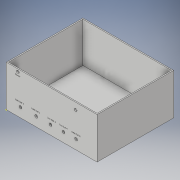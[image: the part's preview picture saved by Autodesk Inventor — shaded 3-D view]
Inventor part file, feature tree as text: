
AUTODESK INVENTOR PART (.ipt)
format: ipt  version: 2019 (Build 230136000, 136)  size: 162,816 bytes
history: native  units: in
note: dims shown in document units (in); Inventor stores cm internally (conversion verified against a paired STEP export)
features: sketch x11, extrude x6, hole x2
ambient origin geometry x8: Origin, YZ Plane, XZ Plane, XY Plane, X Axis, Y Axis, Z Axis, Center Point
bodies: Solid1 (feature_tree)
feature tree (19):
  extrude  "Extrusion1"  Depth=0.1in TaperAngle=0.0deg
  sketch  "Sketch2"  dims[d4=0.1in d5=0.0in d8=0.1in d9=0.0in]
  extrude  "Extrusion2"  Depth=0.1in TaperAngle=0.0deg
  extrude  "Extrusion3"  Depth=0.7004in
  extrude  "Extrusion5"  Depth=0.3034in TaperAngle=0.0deg
  extrude  "Extrusion6"  Depth=6.75in
  sketch  "Sketch9"  dims[d49=0.25in d50=0.75in d51=0.375in d52=0.25in d53=0.5635in d54=0.5in d55=0.0in]
  sketch  "Sketch13"  dims[d56=0.25in d57=0.75in d58=0.375in d59=0.25in d60=0.5635in d61=0.59in d62=0.0in]
  sketch  "Sketch14"
  extrude  "Extrusion8"  [1 undecoded]
  sketch  "Sketch16"
  hole  "Hole4"  [1 undecoded]
  hole  "Hole5"  [1 undecoded]
  sketch  "Sketch1"  dims[d0=0.1in d1=0.0in d2=0.1in d3=0.0in]
  sketch  "Sketch3"  dims[d10=0.1in d11=0.0in d43=0.7004in]
  sketch  "Sketch4"  dims[d44=0.3034in d45=0.2in d46=0.0in]
  sketch  "Sketch6"  dims[d47=8.0in d48=6.75in]
  sketch  "Sketch15"
  sketch  "Sketch17"
note: 3 required parameter values undecoded (feature->parameter linkage not recoverable at this tier; creation-order binding heuristic only, values carry confidence <= 0.55)
